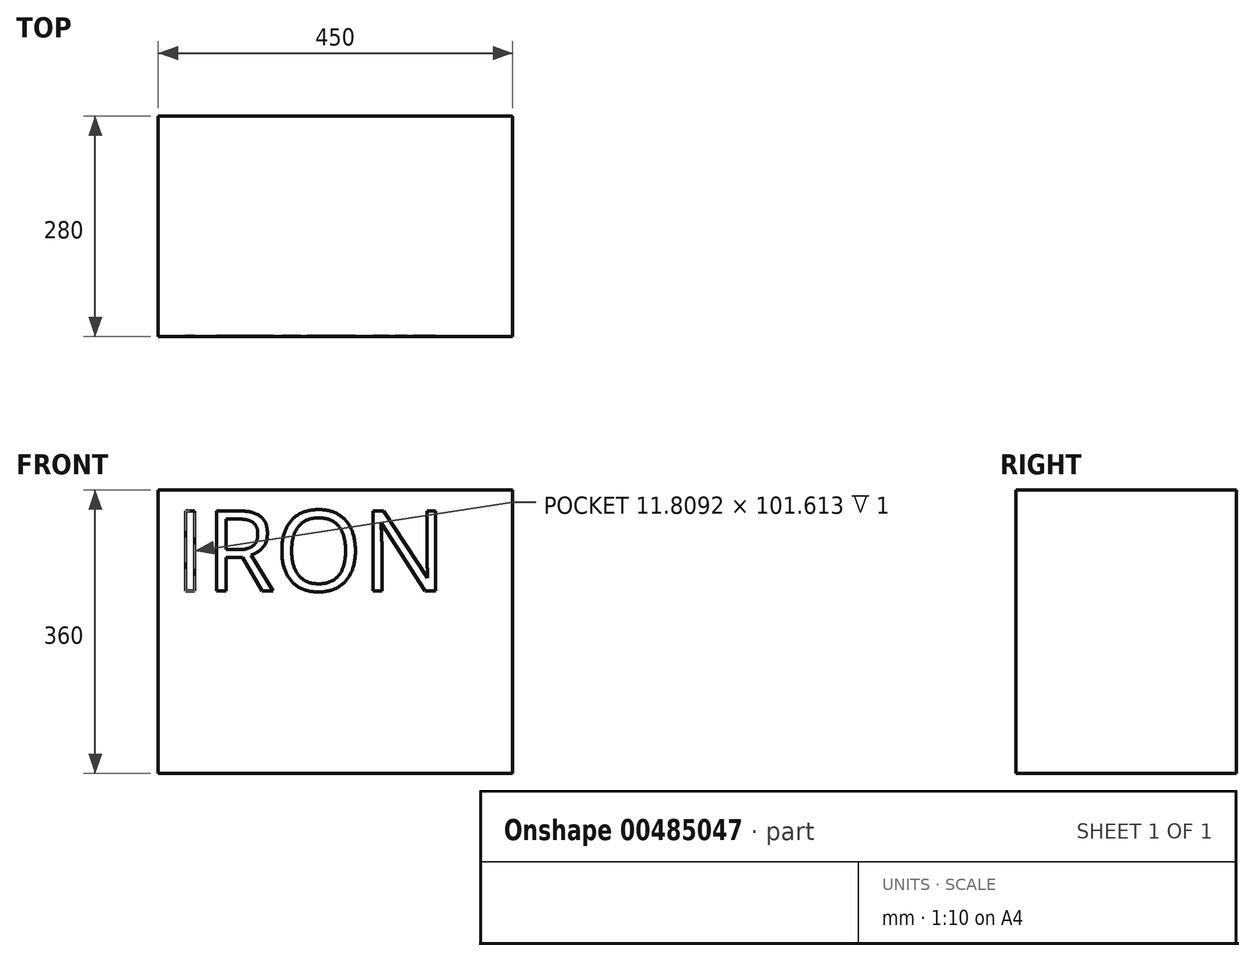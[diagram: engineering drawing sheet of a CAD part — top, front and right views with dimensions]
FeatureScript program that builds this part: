
annotation { "Feature Type Name" : "Feature", "Feature Type Description" : "" }
export const myFeature = defineFeature(function(context is Context, id is Id, definition is map)
    precondition{}
    {
        {
            var Q0;
            Q0=qCreatedBy(makeId("Top.planeOp"),FACE);
            var sketch = newSketch(context, id + "F0", { "sketchPlane" : qUnion([Q0])});
            skLineSegment(sketch, "E0.bottom", {"start": v(225, -140) * mm, "end": v(-225, -140) * mm});
            skLineSegment(sketch, "E0.top", {"start": v(225, 140) * mm, "end": v(-225, 140) * mm});
            skLineSegment(sketch, "E0.left", {"start": v(225, -140) * mm, "end": v(225, 140) * mm});
            skLineSegment(sketch, "E0.right", {"start": v(-225, -140) * mm, "end": v(-225, 140) * mm});
            skPoint(sketch, "E0.middle", {"position": v(0, 0) * mm});
            skSolve(sketch);
        }
        {
            var Q0;
            Q0=makeQuery(id+"F0.imprint","IMPRINT",FACE,{"disambiguationData":[TD([[makeQuery(id+"F0.imprint","IMPRINT",EDGE,{"derivedFrom":sQuery(id+"F0.wireOp",EDGE,"E0.bottom")}),-1.0]])]});
            extrude(context, id + "F1", {"entities" : qUnion([Q0]), "depth" : 360 * mm});
        }
        {
            var Q0;
            Q0=makeQuery(id+"F1.opExtrude","SWEPT_FACE",FACE,{"disambiguationData":[OSD([sQuery(id+"F0.wireOp",EDGE,"E0.bottom")])]});
            var sketch = newSketch(context, id + "F2", { "sketchPlane" : qUnion([Q0])});
            skText(sketch, "E1", { "text": "IRON", "fontName": "OpenSans-Regular.ttf"});
            const initialGuessF2  = {"E1": [-0.20437, 0.23193, 1, 0, 0.10248]};
            skSetInitialGuess(sketch, initialGuessF2);
            skSolve(sketch);
        }
        {
            var Q0;
            Q0 = qSketchRegion(id + "F2", true);
            extrude(context, id + "F3", {"entities" : qUnion([Q0]), "operationType" : NewBodyOperationType.REMOVE, "oppositeDirection" : true, "depth" : 1 * mm});
        }
    });
